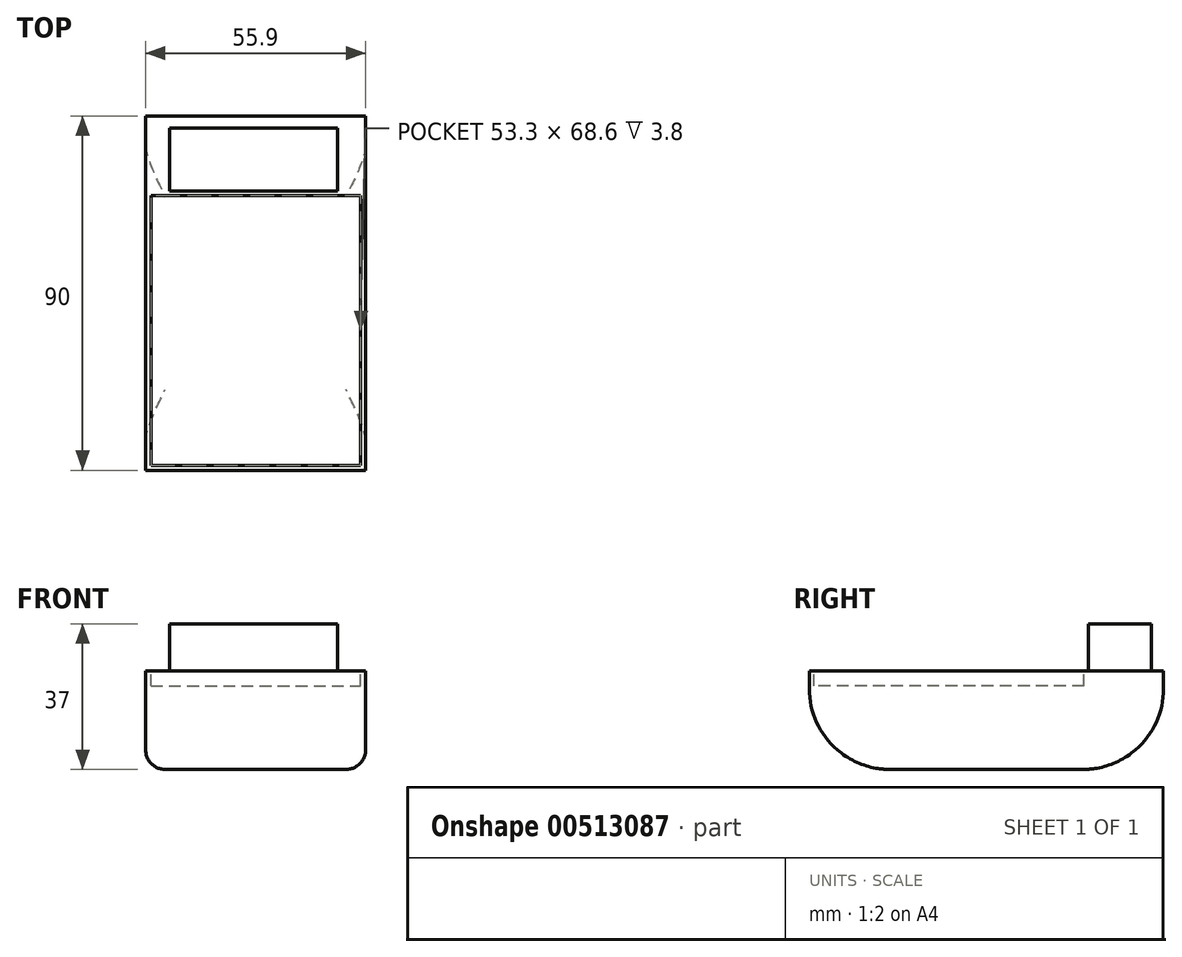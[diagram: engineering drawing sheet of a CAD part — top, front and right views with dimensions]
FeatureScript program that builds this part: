
annotation { "Feature Type Name" : "Feature", "Feature Type Description" : "" }
export const myFeature = defineFeature(function(context is Context, id is Id, definition is map)
    precondition{}
    {
        {
            var Q0;
            Q0=qCreatedBy(makeId("Top.planeOp"),FACE);
            var sketch = newSketch(context, id + "F0", { "sketchPlane" : qUnion([Q0])});
            skLineSegment(sketch, "E0.bottom", {"start": v(-25.79, 44.16) * mm, "end": v(30.11, 44.16) * mm});
            skLineSegment(sketch, "E0.top", {"start": v(-25.79, -45.84) * mm, "end": v(30.11, -45.84) * mm});
            skLineSegment(sketch, "E0.left", {"start": v(-25.79, 44.16) * mm, "end": v(-25.79, -45.84) * mm});
            skLineSegment(sketch, "E0.right", {"start": v(30.11, 44.16) * mm, "end": v(30.11, -45.84) * mm});
            skSolve(sketch);
        }
        {
            var Q0;
            Q0=makeQuery(id+"F0.imprint","IMPRINT",FACE,{"disambiguationData":[TD([[makeQuery(id+"F0.imprint","IMPRINT",EDGE,{"derivedFrom":sQuery(id+"F0.wireOp",EDGE,"E0.bottom")}),-1.0]])]});
            extrude(context, id + "F1", {"entities" : qUnion([Q0]), "depth" : 25 * mm});
        }
        {
            var Q0;
            Q0=makeQuery(id+"F1.opExtrude","CAP_EDGE",EDGE,{"disambiguationData":[OSD([sQuery(id+"F0.wireOp",EDGE,"E0.top")])],"isStart":true});
            var Q1;
            Q1=makeQuery(id+"F1.opExtrude","CAP_EDGE",EDGE,{"disambiguationData":[OSD([sQuery(id+"F0.wireOp",EDGE,"E0.bottom")])],"isStart":true});
            fillet(context, id + "F2", {"entities" : qUnion([Q0, Q1]), "radius" : 20.52 * mm, "tangentPropagation" : true, "allowEdgeOverflow" : false});
        }
        {
            var Q0;
            Q0=makeQuery(id+"F1.opExtrude","CAP_FACE",FACE,{"disambiguationData":[OSD([sQuery(id+"F0.wireOp",EDGE,"E0.bottom"),sQuery(id+"F0.wireOp",EDGE,"E0.top"),sQuery(id+"F0.wireOp",EDGE,"E0.left"),sQuery(id+"F0.wireOp",EDGE,"E0.right")])],"isStart":false});
            var sketch = newSketch(context, id + "F3", { "sketchPlane" : qUnion([Q0])});
            skLineSegment(sketch, "E1.bottom", {"start": v(-24.44, 23.94) * mm, "end": v(28.86, 23.94) * mm});
            skLineSegment(sketch, "E1.top", {"start": v(-24.44, -44.66) * mm, "end": v(28.86, -44.66) * mm});
            skLineSegment(sketch, "E1.left", {"start": v(-24.44, 23.94) * mm, "end": v(-24.44, -44.66) * mm});
            skLineSegment(sketch, "E1.right", {"start": v(28.86, 23.94) * mm, "end": v(28.86, -44.66) * mm});
            skSolve(sketch);
        }
        {
            var Q0;
            Q0=makeQuery(id+"F3.imprint","IMPRINT",FACE,{"disambiguationData":[TD([[makeQuery(id+"F3.imprint","IMPRINT",EDGE,{"derivedFrom":sQuery(id+"F3.wireOp",EDGE,"E1.bottom")}),-1.0]])]});
            extrude(context, id + "F4", {"entities" : qUnion([Q0]), "operationType" : NewBodyOperationType.REMOVE, "oppositeDirection" : true, "depth" : 3.8 * mm, "offsetDistance" : 25 * mm});
        }
        {
            var Q0;
            Q0=makeQuery(id+"F1.opExtrude","CAP_EDGE",EDGE,{"disambiguationData":[OSD([sQuery(id+"F0.wireOp",EDGE,"E0.right")])],"isStart":true});
            fillet(context, id + "F5", {"entities" : qUnion([Q0]), "radius" : 5 * mm, "allowEdgeOverflow" : false});
        }
        {
            var Q0;
            Q0=makeQuery(id+"F1.opExtrude","CAP_EDGE",EDGE,{"disambiguationData":[OSD([sQuery(id+"F0.wireOp",EDGE,"E0.left")])],"isStart":true});
            fillet(context, id + "F6", {"entities" : qUnion([Q0]), "radius" : 5 * mm, "allowEdgeOverflow" : false});
        }
        {
            var Q0;
            Q0=makeQuery(id+"F1.opExtrude","CAP_FACE",FACE,{"disambiguationData":[OSD([sQuery(id+"F0.wireOp",EDGE,"E0.bottom"),sQuery(id+"F0.wireOp",EDGE,"E0.top"),sQuery(id+"F0.wireOp",EDGE,"E0.left"),sQuery(id+"F0.wireOp",EDGE,"E0.right")])],"isStart":false});
            var sketch = newSketch(context, id + "F7", { "sketchPlane" : qUnion([Q0])});
            skLineSegment(sketch, "E2.bottom", {"start": v(-19.72, 41.09) * mm, "end": v(22.95, 41.09) * mm});
            skLineSegment(sketch, "E2.top", {"start": v(-19.72, 25.05) * mm, "end": v(22.93, 25.05) * mm});
            skLineSegment(sketch, "E2.left", {"start": v(-19.72, 41.09) * mm, "end": v(-19.72, 25.05) * mm});
            skPoint(sketch, "E3.endSnap0", {"position": v(1.6, 25.05) * mm});
            skLineSegment(sketch, "E4", {"start": v(22.93, 25.05) * mm, "end": v(22.95, 41.09) * mm});
            skSolve(sketch);
        }
        {
            var Q0;
            Q0=makeQuery(id+"F7.imprint","IMPRINT",FACE,{"disambiguationData":[TD([[makeQuery(id+"F7.imprint","IMPRINT",EDGE,{"derivedFrom":sQuery(id+"F7.wireOp",EDGE,"E2.bottom")}),-1.0]])]});
            extrude(context, id + "F8", {"entities" : qUnion([Q0]), "operationType" : NewBodyOperationType.ADD, "depth" : 12 * mm, "offsetDistance" : 25 * mm});
        }
    });
